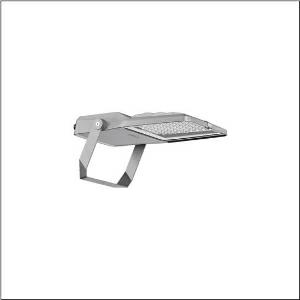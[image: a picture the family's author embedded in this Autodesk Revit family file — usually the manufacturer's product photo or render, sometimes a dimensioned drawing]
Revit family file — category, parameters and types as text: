
# Revit family: floodlight_fl_21_mini___pl43_5xa7776c2a1a_c133
name_source: partatom
category: Lighting Fixtures
units: mm (PartAtom-declared; Revit-internal decimal feet)

## family parameters
Cut with Voids When Loaded = No
Host = Face
Light Source = No
Part Type = Normal
Room Calculation Point = No
Round Connector Dimension = Use Diameter
Shared = No

## types (1)
- --- (1 x LED, 12500 lm, 89 W, 3000K)
    Apparent Load = 89 VA
    CIE Flux Codes = 27 78 99 100 100
    Color Rendering = 70
    Color Temperature = 3000K
    Default Elevation = 1800 mm
    Description = Floodlight FL 21 mini, floodlight, primary light control with lens, of PMMA, primary optical cover: protective disc, of toughened safety glass, transparent, light distribution: PL43, light emission: direct distribution, installation type: surface-mounted, LED, High Power LED, rated luminous flux: 12.500lm, luminous efficacy: 140lm/W, light colour: 730, colour temperature: 3000K, control gear: Smart Interface (Zhaga), control: flexible luminous flux parameterisation, time-dependent luminous flux control, constant luminous flux control, overheat protection, pre-setting: logarithmic dimming characteristic, with terminal, 6-pole, mains connection: 220..240V, AC, 50/60Hz, start of lifetime: 89W, end of service life: 94W, reduction: 43W, luminaire housing, of diecast aluminium, powder-coated, Siteco® metallic grey (DB 702S), corrosivity category C5 mid according to DIN EN ISO 12944, suitable for swimming pools, chlorine-resistant, sealing non-destructively replaceable, mounting bracket, of steel, galvanised, powder-coated, Siteco® metallic grey (DB 702S), Smart Interface below and above, protection rating (complete): IP66, insulation class (complete): insulation class II (safety insulation), certification: CE, ENEC, VDE, protection symbol: D, impact resistance: IK08, permissible operating ambient temperature: -40..+40°C, permissible operating ambient temperature for outdoor applications: -40..+50°C, standard: DIN EN 12944, LABS conformity tested according to VDMA 24364:2018-05, packaging unit: 1 piece

Light Distribution: PL43
    Height = 70 mm
    Lamp = 1 x LED
    Lamp Light Flux = 12500 lm
    Lamp Power = 89 W
    Lamp count = 1
    Length = 485 mm
    Luminous efficacy = 140 lm/W
    Manufacturer = Siteco
    ModVariant = No
    Model = 5XA7776C2A1A
    Number of Poles = 1
    OnlyDefault = Yes
    Power Factor = 1
    Product Name = Floodlight FL 21 mini | PL43
    Product group = floodlight | pylon annexe
    ProductGroupID = 6200
    Protection Class = Protection class II
    Protection Degree = IP 66
    RLX_Detail_Level = 1
    RLX_Emergency_Light_Flux = 0 lm
    RLX_Emergency_Type = 0
    RLX_Emergency_Type_DB = No
    RlxData = <blob elided: 95741 chars, md5=37ef8911>
    Socket = socket
    Standby Power = 0 W
    System Light Flux = 12500 lm
    System Power = 89 W
    Type Comments = factory setting: luminous flux: 100 % | dim-lin: 254 | 456 mA
    Type Image = l_1006845.jpg
    URL = http://relux.com
    VarID = @adj_161160
    Voltage = 0 V
    Weight = 0.00 kg
    Width = 337 mm

## geometry (parser evidence)
native form markers: Blend x4, Sweep x10
no freeform markers — native parametric forms only
